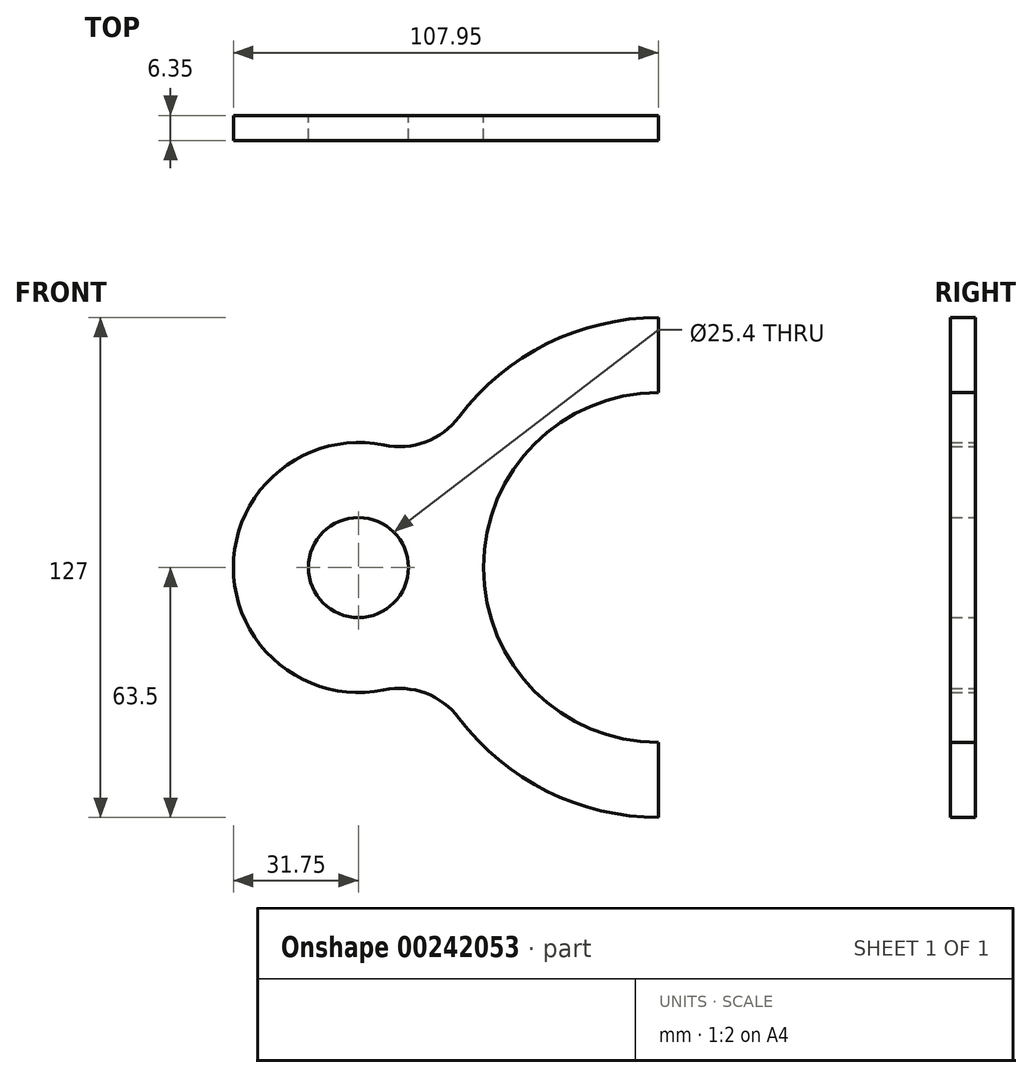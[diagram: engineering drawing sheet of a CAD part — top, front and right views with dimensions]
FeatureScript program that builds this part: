
annotation { "Feature Type Name" : "Feature", "Feature Type Description" : "" }
export const myFeature = defineFeature(function(context is Context, id is Id, definition is map)
    precondition{}
    {
        {
            var Q0;
            Q0=qCreatedBy(makeId("Front.planeOp"),FACE);
            var sketch = newSketch(context, id + "F0", { "sketchPlane" : qUnion([Q0])});
            skCircle(sketch, "E0", {"center": v(0, 0) * mm, "radius": 44.45 * mm});
            skArc(sketch, "E1", {"start": v(-50.65, -38.3) * mm, "mid": v(0, -63.5) * mm, "end": v(50.65, -38.3) * mm});
            skArc(sketch, "E2", {"start": v(-69.75, 31.09) * mm, "mid": v(-107.95, 0.02) * mm, "end": v(-69.79, -31.1) * mm});
            skLineSegment(sketch, "E3", {"start": v(0, 63.5) * mm, "end": v(0, -63.5) * mm});
            skArc(sketch, "E4.MirrorC", {"start": v(69.75, 31.09) * mm, "mid": v(107.95, 0.02) * mm, "end": v(69.79, -31.1) * mm});
            skCircle(sketch, "E5", {"center": v(-76.2, 0) * mm, "radius": 12.7 * mm});
            skCircle(sketch, "E6.MirrorC", {"center": v(76.2, 0) * mm, "radius": 12.7 * mm});
            skArc(sketch, "E7.MirrorC", {"start": v(-69.79, -31.1) * mm, "mid": v(-59.18, -31.93) * mm, "end": v(-50.65, -38.3) * mm});
            skArc(sketch, "E8.MirrorC", {"start": v(69.79, -31.1) * mm, "mid": v(59.18, -31.93) * mm, "end": v(50.65, -38.3) * mm});
            skArc(sketch, "E9.MirrorC", {"start": v(-69.75, 31.09) * mm, "mid": v(-59.17, 31.91) * mm, "end": v(-50.68, 38.26) * mm});
            skArc(sketch, "E10.MirrorC", {"start": v(69.75, 31.09) * mm, "mid": v(59.17, 31.91) * mm, "end": v(50.68, 38.26) * mm});
            skArc(sketch, "E11.trimOffspring", {"start": v(50.68, 38.26) * mm, "mid": v(0, 63.5) * mm, "end": v(-50.68, 38.26) * mm});
            skSolve(sketch);
        }
        {
            var Q0;
            Q0=makeQuery(id+"F0.imprint","IMPRINT",FACE,{"disambiguationData":[TD([[makeQuery(id+"F0.imprint","IMPRINT",EDGE,{"derivedFrom":sQuery(id+"F0.wireOp",EDGE,"E4.MirrorC")}),-1.0]])]});
            var Q1;
            Q1=makeQuery(id+"F0.imprint","IMPRINT",FACE,{"disambiguationData":[TD([[makeQuery(id+"F0.imprint","IMPRINT",EDGE,{"derivedFrom":sQuery(id+"F0.wireOp",EDGE,"E2")}),1.0]])]});
            extrude(context, id + "F1", {"entities" : qUnion([Q0, Q1]), "depth" : 6.35 * mm});
        }
    });
